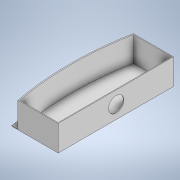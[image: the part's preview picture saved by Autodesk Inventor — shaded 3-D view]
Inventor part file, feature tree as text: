
AUTODESK INVENTOR PART (.ipt)
format: ipt  version: 2020.2 (Build 242310000, 310)  size: 223,744 bytes
history: native  units: mm
features: extrude x11, sketch x11
ambient origin geometry x8: Origin, YZ Plane, XZ Plane, XY Plane, X Axis, Y Axis, Z Axis, Center Point
bodies: Solide1 (feature_tree)
feature tree (22):
  extrude  "Extrusion1"  Depth=301.169mm
  extrude  "Extrusion2"  Depth=65.0mm TaperAngle=0.0deg
  extrude  "Extrusion3"  Depth=10.0mm TaperAngle=0.0deg
  extrude  "Extrusion4"  Depth=10.0mm TaperAngle=0.0deg
  extrude  "Extrusion5"  Depth=2.0mm
  extrude  "Extrusion6"  Depth=2.0mm
  extrude  "Extrusion7"  Depth=100.0mm TaperAngle=0.0deg
  extrude  "Extrusion8"  Depth=2.0mm TaperAngle=0.0deg
  extrude  "Extrusion9"  Depth=2.0mm TaperAngle=0.0deg
  extrude  "Extrusion10"  Depth=30.0mm TaperAngle=0.0deg
  extrude  "Extrusion11"  Depth=65.0mm TaperAngle=0.0deg
  sketch  "Esquisse1"
  sketch  "Esquisse2"
  sketch  "Esquisse3"
  sketch  "Esquisse4"
  sketch  "Esquisse5"
  sketch  "Esquisse7"
  sketch  "Esquisse8"
  sketch  "Esquisse9"
  sketch  "Esquisse10"
  sketch  "Esquisse11"
  sketch  "Esquisse12"
